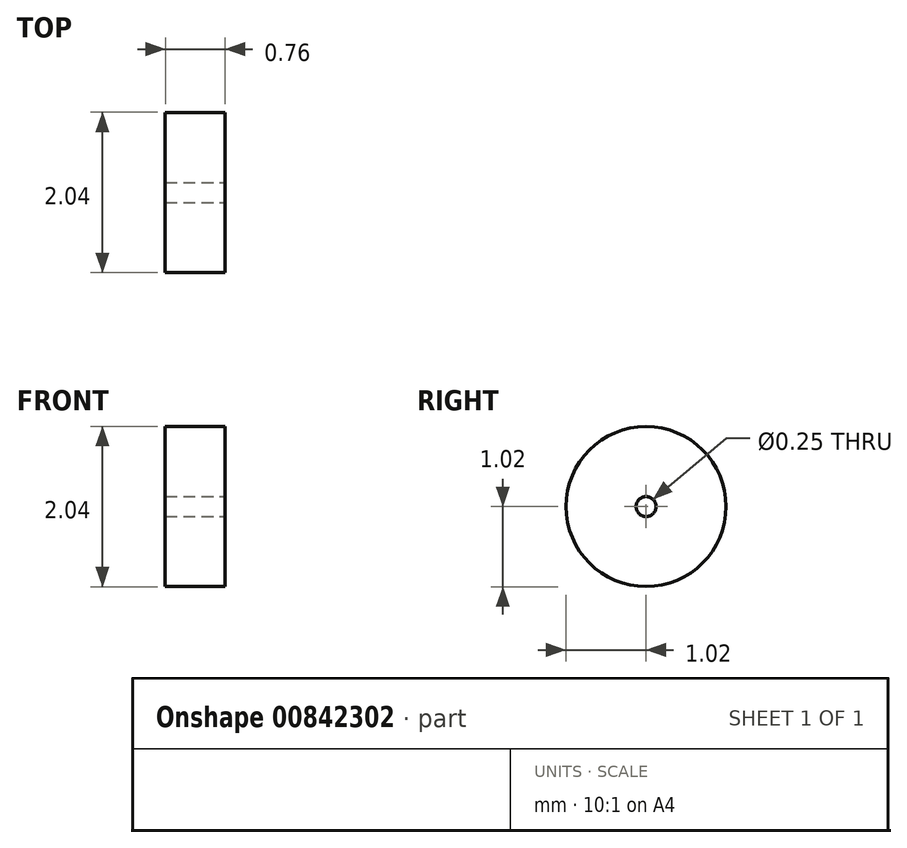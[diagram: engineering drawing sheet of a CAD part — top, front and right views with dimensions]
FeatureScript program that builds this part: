
annotation { "Feature Type Name" : "Feature", "Feature Type Description" : "" }
export const myFeature = defineFeature(function(context is Context, id is Id, definition is map)
    precondition{}
    {
        {
            var Q0;
            Q0=qCreatedBy(makeId("Right.planeOp"),FACE);
            var sketch = newSketch(context, id + "F0", { "sketchPlane" : qUnion([Q0])});
            skCircle(sketch, "E0", {"center": v(0, 0) * mm, "radius": 1.02 * mm});
            skSolve(sketch);
        }
        {
            var Q0;
            Q0 = qSketchRegion(id + "F0", true);
            extrude(context, id + "F1", {"entities" : qUnion([Q0]), "depth" : 0.38 * mm, "offsetDistance" : 25.4 * mm, "hasSecondDirection" : true, "secondDirectionOppositeDirection" : true, "secondDirectionDepth" : 0.38 * mm});
        }
        {
            var Q0;
            Q0=makeQuery(id+"F1.opExtrude","CAP_FACE",FACE,{"disambiguationData":[OSD([sQuery(id+"F0.wireOp",EDGE,"E0")])],"isStart":false});
            var sketch = newSketch(context, id + "F2", { "sketchPlane" : qUnion([Q0])});
            skCircle(sketch, "E1", {"center": v(0, 0) * mm, "radius": 0.13 * mm});
            skSolve(sketch);
        }
        {
            var Q0;
            Q0 = qSketchRegion(id + "F2", true);
            extrude(context, id + "F3", {"entities" : qUnion([Q0]), "operationType" : NewBodyOperationType.REMOVE, "endBound" : BoundingType.THROUGH_ALL, "oppositeDirection" : true, "depth" : 25.4 * mm, "offsetDistance" : 25.4 * mm});
        }
    });
